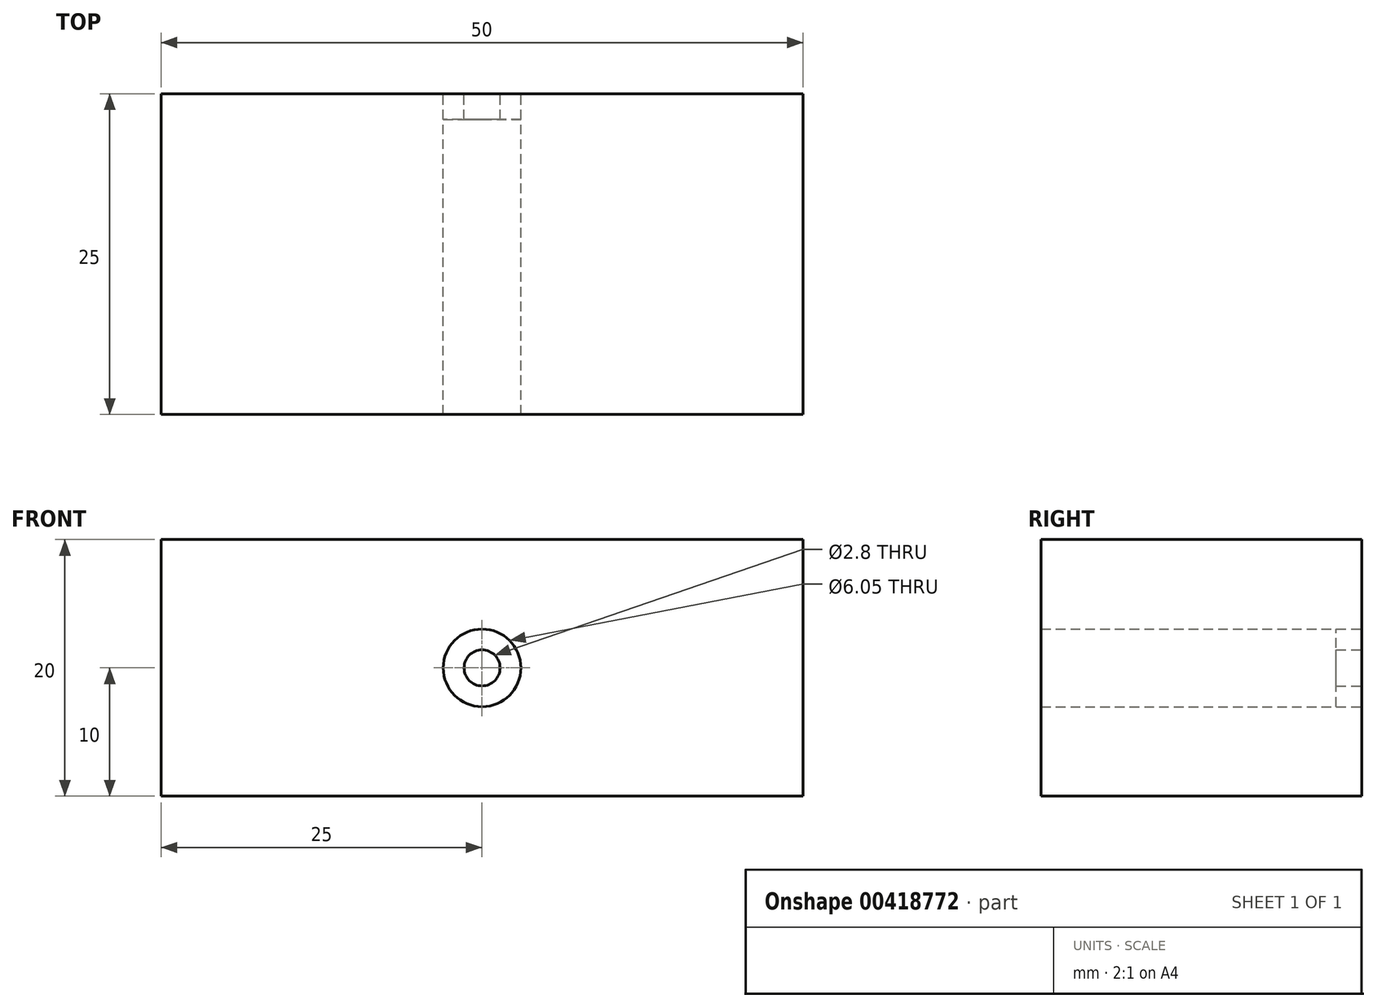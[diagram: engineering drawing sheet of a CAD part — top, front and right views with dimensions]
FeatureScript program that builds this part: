
annotation { "Feature Type Name" : "Feature", "Feature Type Description" : "" }
export const myFeature = defineFeature(function(context is Context, id is Id, definition is map)
    precondition{}
    {
        {
            var Q0;
            Q0=qCreatedBy(makeId("Front.planeOp"),FACE);
            var sketch = newSketch(context, id + "F0", { "sketchPlane" : qUnion([Q0])});
            skCircle(sketch, "E0", {"center": v(0, 0) * mm, "radius": 3.02 * mm});
            skLineSegment(sketch, "E1.bottom", {"start": v(25, 10) * mm, "end": v(-25, 10) * mm});
            skLineSegment(sketch, "E1.top", {"start": v(25, -10) * mm, "end": v(-25, -10) * mm});
            skLineSegment(sketch, "E1.left", {"start": v(25, 10) * mm, "end": v(25, -10) * mm});
            skLineSegment(sketch, "E1.right", {"start": v(-25, 10) * mm, "end": v(-25, -10) * mm});
            skCircle(sketch, "E2", {"center": v(0, 0) * mm, "radius": 1.4 * mm});
            skSolve(sketch);
        }
        {
            var Q0;
            Q0=makeQuery(id+"F0.imprint","IMPRINT",FACE,{"disambiguationData":[TD([[makeQuery(id+"F0.imprint","IMPRINT",EDGE,{"derivedFrom":sQuery(id+"F0.wireOp",EDGE,"E0")}),-1.0]])]});
            extrude(context, id + "F1", {"entities" : qUnion([Q0]), "depth" : 25 * mm});
        }
        {
            var Q0;
            Q0=sQuery(id+"F0.wireOp",EDGE,"E0");
            extrude(context, id + "F2", {"bodyType" : ToolBodyType.SURFACE, "surfaceEntities" : qUnion([Q0]), "depth" : 2 * mm});
        }
        {
            var Q0;
            Q0=makeQuery(id+"F0.imprint","IMPRINT",FACE,{"disambiguationData":[TD([[makeQuery(id+"F0.imprint","IMPRINT",EDGE,{"derivedFrom":sQuery(id+"F0.wireOp",EDGE,"E0")}),1.0]])]});
            extrude(context, id + "F3", {"entities" : qUnion([Q0]), "depth" : 2 * mm});
        }
    });
